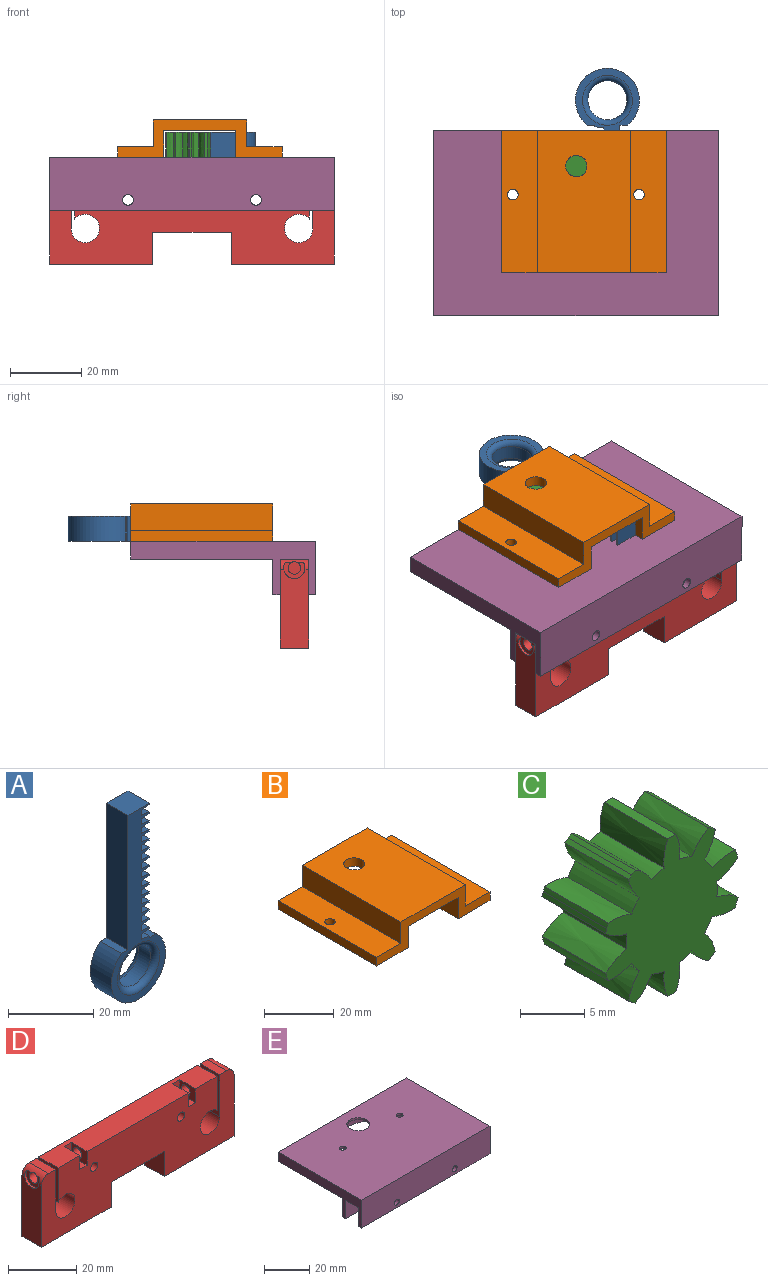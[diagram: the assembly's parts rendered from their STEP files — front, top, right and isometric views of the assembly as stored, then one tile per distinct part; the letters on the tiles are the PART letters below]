
ASSEMBLY  parts=5 mates=10
PART A: 71 faces, bbox 18x7x54.7 mm
  f0: plane 7x0.45mm, normal (1,0,0), area 3.1mm2, adj f15,f16,f60,f62
  f1: plane 7x0.45mm, normal (1,0,0), area 3.1mm2, adj f15,f16,f57,f59
  f2: plane 7x0.45mm, normal (1,0,0), area 3.2mm2, adj f15,f16,f54,f56
  f3: plane 7x0.45mm, normal (1,0,0), area 3.2mm2, adj f15,f16,f51,f53
  f4: plane 7x0.45mm, normal (1,0,0), area 3.2mm2, adj f15,f16,f48,f50
  f5: plane 7x0.45mm, normal (1,0,0), area 3.1mm2, adj f15,f16,f45,f47
  f6: plane 7x0.45mm, normal (1,0,0), area 3.1mm2, adj f15,f16,f42,f44
  f7: plane 7x0.45mm, normal (1,0,0), area 3.1mm2, adj f15,f16,f39,f41
  f8: plane 7x0.45mm, normal (1,0,0), area 3.1mm2, adj f15,f16,f36,f38
  f9: plane 7x0.45mm, normal (1,0,0), area 3.2mm2, adj f15,f16,f33,f35
  f10: plane 7x0.45mm, normal (1,0,0), area 3.1mm2, adj f15,f16,f30,f32
  f11: plane 7x0.45mm, normal (1,0,0), area 3.1mm2, adj f15,f16,f27,f29
  f12: plane 7x0.45mm, normal (1,0,0), area 3.1mm2, adj f15,f16,f24,f26
  f13: plane 7x0.45mm, normal (1,0,0), area 3.2mm2, adj f15,f16,f21,f23
  f14: plane 7x0.45mm, normal (1,0,0), area 3.1mm2, adj f15,f16,f20,f66
  f15: plane 54.7x18mm, normal (0,1,0), area 288.5mm2, adj f0,f1,f2,f3,f4,f5,f6,f7
  f16: plane 54.7x18mm, normal (0,-1,0), area 288.5mm2, adj f0,f1,f2,f3,f4,f5,f6,f7
  f17: plane 7x0.45mm, normal (1,0,0), area 3.1mm2, adj f15,f16,f19,f63
  f18: plane 38.7x7mm, normal (-1,0,0), area 270.9mm2, adj f15,f16,f19,f65
  f19: plane 7x7mm, normal (0,0,1), area 49mm2, adj f15,f16,f17,f18
  f20: plane 7x2.5mm, normal (0.12,0,0.99), area 17.6mm2, adj f14,f15,f16,f22
  f21: plane 7x2.5mm, normal (0.12,0,-0.99), area 17.6mm2, adj f13,f15,f16,f22
  f22: plane 7x1.5mm, normal (1,0,0), area 10.5mm2, adj f15,f16,f20,f21
  f23: plane 7x2.5mm, normal (0.12,0,0.99), area 17.6mm2, adj f13,f15,f16,f25
  f24: plane 7x2.5mm, normal (0.12,0,-0.99), area 17.6mm2, adj f12,f15,f16,f25
  f25: plane 7x1.5mm, normal (1,0,0), area 10.5mm2, adj f15,f16,f23,f24
  f26: plane 7x2.5mm, normal (0.12,0,0.99), area 17.6mm2, adj f12,f15,f16,f28
  f27: plane 7x2.5mm, normal (0.12,0,-0.99), area 17.6mm2, adj f11,f15,f16,f28
  f28: plane 7x1.5mm, normal (1,0,0), area 10.5mm2, adj f15,f16,f26,f27
  f29: plane 7x2.5mm, normal (0.12,0,0.99), area 17.6mm2, adj f11,f15,f16,f31
  f30: plane 7x2.5mm, normal (0.12,0,-0.99), area 17.6mm2, adj f10,f15,f16,f31
  f31: plane 7x1.5mm, normal (1,0,0), area 10.5mm2, adj f15,f16,f29,f30
  f32: plane 7x2.5mm, normal (0.12,0,0.99), area 17.6mm2, adj f10,f15,f16,f34
  f33: plane 7x2.5mm, normal (0.12,0,-0.99), area 17.6mm2, adj f9,f15,f16,f34
  f34: plane 7x1.5mm, normal (1,0,0), area 10.5mm2, adj f15,f16,f32,f33
  f35: plane 7x2.5mm, normal (0.12,0,0.99), area 17.6mm2, adj f9,f15,f16,f37
  f36: plane 7x2.5mm, normal (0.12,0,-0.99), area 17.6mm2, adj f8,f15,f16,f37
  f37: plane 7x1.5mm, normal (1,0,0), area 10.5mm2, adj f15,f16,f35,f36
  f38: plane 7x2.5mm, normal (0.12,0,0.99), area 17.6mm2, adj f8,f15,f16,f40
  f39: plane 7x2.5mm, normal (0.12,0,-0.99), area 17.6mm2, adj f7,f15,f16,f40
  f40: plane 7x1.5mm, normal (1,0,0), area 10.5mm2, adj f15,f16,f38,f39
  f41: plane 7x2.5mm, normal (0.12,0,0.99), area 17.6mm2, adj f7,f15,f16,f43
  f42: plane 7x2.5mm, normal (0.12,0,-0.99), area 17.6mm2, adj f6,f15,f16,f43
  f43: plane 7x1.5mm, normal (1,0,0), area 10.5mm2, adj f15,f16,f41,f42
  f44: plane 7x2.5mm, normal (0.12,0,0.99), area 17.6mm2, adj f6,f15,f16,f46
  f45: plane 7x2.5mm, normal (0.12,0,-0.99), area 17.6mm2, adj f5,f15,f16,f46
  f46: plane 7x1.5mm, normal (1,0,0), area 10.5mm2, adj f15,f16,f44,f45
  f47: plane 7x2.5mm, normal (0.12,0,0.99), area 17.6mm2, adj f5,f15,f16,f49
  f48: plane 7x2.5mm, normal (0.12,0,-0.99), area 17.6mm2, adj f4,f15,f16,f49
  f49: plane 7x1.5mm, normal (1,0,0), area 10.5mm2, adj f15,f16,f47,f48
  f50: plane 7x2.5mm, normal (0.12,0,0.99), area 17.6mm2, adj f4,f15,f16,f52
  f51: plane 7x2.5mm, normal (0.12,0,-0.99), area 17.6mm2, adj f3,f15,f16,f52
  f52: plane 7x1.5mm, normal (1,0,0), area 10.5mm2, adj f15,f16,f50,f51
  f53: plane 7x2.5mm, normal (0.12,0,0.99), area 17.6mm2, adj f3,f15,f16,f55
  f54: plane 7x2.5mm, normal (0.12,0,-0.99), area 17.6mm2, adj f2,f15,f16,f55
  f55: plane 7x1.5mm, normal (1,0,0), area 10.5mm2, adj f15,f16,f53,f54
  f56: plane 7x2.5mm, normal (0.12,0,0.99), area 17.6mm2, adj f2,f15,f16,f58
  f57: plane 7x2.5mm, normal (0.12,0,-0.99), area 17.6mm2, adj f1,f15,f16,f58
  f58: plane 7x1.5mm, normal (1,0,0), area 10.5mm2, adj f15,f16,f56,f57
  f59: plane 7x2.5mm, normal (0.12,0,0.99), area 17.6mm2, adj f1,f15,f16,f61
  f60: plane 7x2.5mm, normal (0.12,0,-0.99), area 17.6mm2, adj f0,f15,f16,f61
  f61: plane 7x1.5mm, normal (1,0,0), area 10.5mm2, adj f15,f16,f59,f60
  f62: plane 7x2.5mm, normal (0.12,0,0.99), area 17.6mm2, adj f0,f15,f16,f64
  f63: plane 7x2.5mm, normal (0.12,0,-0.99), area 17.6mm2, adj f15,f16,f17,f64
  f64: plane 7x1.5mm, normal (1,0,0), area 10.5mm2, adj f15,f16,f62,f63
  f65: plane 7x2.16mm, normal (0,0,1), area 15.1mm2, adj f15,f16,f18,f68
  f66: plane 7x2.16mm, normal (0,0,1), area 15.1mm2, adj f14,f15,f16,f68
  f67: cylinder r=5.5mm len=11mm, axis (0,-1,0), area 138.2mm2, adj f69,f70
  f68: cylinder r=9mm len=18mm, axis (0,-1,0), area 310.2mm2, adj f15,f16,f65,f66
  f69: torus R=7mm, axis (0,-1,0), area 89.5mm2, adj f16,f67
  f70: torus R=7mm, axis (0,-1,0), area 89.5mm2, adj f15,f67
PART B: 17 faces, bbox 46.3x40x10.5 mm
  f0: plane 40x3mm, normal (-1,0,0), area 120mm2, adj f1,f11,f12,f13
  f1: plane 40x13mm, normal (0,0,-1), area 512.9mm2, adj f0,f2,f12,f13,f15
  f2: plane 40x7.5mm, normal (1,0,0), area 300mm2, adj f1,f3,f12,f13
  f3: plane 40x20.25mm, normal (0,0,-1), area 781.7mm2, adj f2,f4,f12,f13,f14
  f4: plane 40x7.5mm, normal (-1,0,0), area 300mm2, adj f3,f5,f12,f13
  f5: plane 40x13mm, normal (0,0,-1), area 512.9mm2, adj f4,f6,f12,f13,f16
  f6: plane 40x3mm, normal (1,0,0), area 120mm2, adj f5,f7,f12,f13
  f7: plane 40x10mm, normal (0,0,1), area 392.9mm2, adj f6,f8,f12,f13,f16
  f8: plane 40x7.5mm, normal (1,0,0), area 300mm2, adj f7,f9,f12,f13
  f9: plane 40x26.25mm, normal (0,0,1), area 1021.7mm2, adj f8,f10,f12,f13,f14
  f10: plane 40x7.5mm, normal (-1,0,0), area 300mm2, adj f9,f11,f12,f13
  f11: plane 40x10mm, normal (0,0,1), area 392.9mm2, adj f0,f10,f12,f13,f15
  f12: plane 46.25x10.5mm, normal (0,-1,0), area 183.8mm2, adj f0,f1,f2,f3,f4,f5,f6,f7
  f13: plane 46.25x10.5mm, normal (0,1,0), area 183.7mm2, adj f0,f1,f2,f3,f4,f5,f6,f7
  f14: cylinder r=3mm len=6mm, axis (0,0,1), area 56.5mm2, adj f3,f9
  f15: cylinder r=1.5mm len=3mm, axis (0,0,-1), area 28.3mm2, adj f1,f11
  f16: cylinder r=1.5mm len=3mm, axis (0,0,-1), area 28.3mm2, adj f5,f7
PART C: 45 faces, bbox 14.5x7x15 mm
  f0: extruded ~7x2.3mm, area 18.3mm2, adj f1,f42,f43,f44
  f1: cylinder r=7.5mm len=7mm, axis (0,1,0), area 6.4mm2, adj f0,f2,f43,f44
  f2: extruded ~7x1.84mm, area 18.3mm2, adj f1,f3,f43,f44
  f3: cylinder r=5mm len=7mm, axis (0,1,0), area 10mm2, adj f2,f4,f43,f44
  f4: extruded ~7x2.56mm, area 18.3mm2, adj f3,f5,f43,f44
  f5: cylinder r=7.5mm len=7mm, axis (0,1,0), area 6.4mm2, adj f4,f6,f43,f44
  f6: extruded ~7x2.56mm, area 18.3mm2, adj f5,f7,f43,f44
  f7: cylinder r=5mm len=7mm, axis (0,1,0), area 10mm2, adj f6,f8,f43,f44
  f8: extruded ~7x1.84mm, area 18.3mm2, adj f7,f9,f43,f44
  f9: cylinder r=7.5mm len=7mm, axis (0,1,0), area 6.4mm2, adj f8,f10,f43,f44
  f10: extruded ~7x2.3mm, area 18.3mm2, adj f9,f11,f43,f44
  f11: cylinder r=5mm len=7mm, axis (0,1,0), area 10mm2, adj f10,f12,f43,f44
  f12: extruded ~7x2.56mm, area 18.3mm2, adj f11,f13,f43,f44
  f13: cylinder r=7.5mm len=7mm, axis (0,1,0), area 3.2mm2, adj f12,f14,f43,f44
  f14: plane 7x0.43mm, normal (0.95,0,-0.31), area 3.1mm2, adj f13,f15,f43,f44
  f15: extruded ~7x2.32mm, area 18.4mm2, adj f14,f16,f43,f44
  f16: cylinder r=5mm len=7mm, axis (0,1,0), area 10mm2, adj f15,f17,f43,f44
  f17: extruded ~7x2.31mm, area 18.3mm2, adj f16,f18,f43,f44
  f18: cylinder r=7.5mm len=7mm, axis (0,1,0), area 6.4mm2, adj f17,f19,f43,f44
  f19: extruded ~7x2.56mm, area 18.3mm2, adj f18,f20,f43,f44
  f20: cylinder r=5mm len=7mm, axis (0,1,0), area 10mm2, adj f19,f21,f43,f44
  f21: extruded ~7x2.3mm, area 18.3mm2, adj f20,f22,f43,f44
  f22: cylinder r=7.5mm len=7mm, axis (0,1,0), area 6.4mm2, adj f21,f23,f43,f44
  f23: extruded ~7x1.84mm, area 18.3mm2, adj f22,f24,f43,f44
  f24: cylinder r=5mm len=7mm, axis (0,1,0), area 10mm2, adj f23,f25,f43,f44
  f25: extruded ~7x2.57mm, area 18.4mm2, adj f24,f26,f43,f44
  f26: plane 7x0.9mm, normal (0,0,1), area 6.3mm2, adj f25,f27,f43,f44
  f27: extruded ~7x2.57mm, area 18.4mm2, adj f26,f28,f43,f44
  f28: cylinder r=5mm len=7mm, axis (0,1,0), area 10mm2, adj f27,f29,f43,f44
  f29: extruded ~7x1.84mm, area 18.3mm2, adj f28,f30,f43,f44
  f30: cylinder r=7.5mm len=7mm, axis (0,1,0), area 3.2mm2, adj f29,f31,f43,f44
  f31: plane 7x0.36mm, normal (-0.59,0,0.81), area 3.2mm2, adj f30,f32,f43,f44
  f32: extruded ~7x2.32mm, area 18.4mm2, adj f31,f33,f43,f44
  f33: cylinder r=5mm len=7mm, axis (0,1,0), area 10mm2, adj f32,f34,f43,f44
  f34: extruded ~7x2.56mm, area 18.3mm2, adj f33,f35,f43,f44
  f35: cylinder r=7.5mm len=7mm, axis (0,1,0), area 3.2mm2, adj f34,f36,f43,f44
  f36: plane 7x0.43mm, normal (-0.95,0,0.31), area 3.1mm2, adj f35,f37,f43,f44
  f37: extruded ~7x2.32mm, area 18.4mm2, adj f36,f38,f43,f44
  f38: cylinder r=5mm len=7mm, axis (0,1,0), area 10mm2, adj f37,f39,f43,f44
  f39: extruded ~7x2.31mm, area 18.3mm2, adj f38,f40,f43,f44
  f40: cylinder r=7.5mm len=7mm, axis (0,1,0), area 6.4mm2, adj f39,f41,f43,f44
  f41: extruded ~7x2.56mm, area 18.3mm2, adj f40,f42,f43,f44
  f42: cylinder r=5mm len=7mm, axis (0,1,0), area 10mm2, adj f0,f41,f43,f44
  f43: plane 15x14.54mm, normal (0,-1,0), area 117.2mm2, adj f0,f1,f2,f3,f4,f5,f6,f7
  f44: plane 15x14.54mm, normal (0,1,0), area 117.2mm2, adj f0,f1,f2,f3,f4,f5,f6,f7
PART D: 42 faces, bbox 80x8x25 mm
  f0: cylinder r=3mm len=8mm, axis (0,-1,0), area 24.4mm2, adj f2,f3,f17,f18,f36,f40,f41
  f1: plane 22x8mm, normal (-1,0,0), area 164.8mm2, adj f2,f3,f12,f33,f34
  f2: plane 80x25mm, normal (0,-1,0), area 1627.1mm2, adj f0,f1,f4,f5,f6,f7,f8,f9
  f3: plane 80x25mm, normal (0,1,0), area 1657.1mm2, adj f0,f1,f4,f5,f6,f7,f8,f9
  f4: plane 66x8mm, normal (0,0,1), area 489mm2, adj f2,f3,f7,f8,f19,f20,f22,f23
  f5: plane 15x8mm, normal (-1,0,0), area 110.4mm2, adj f2,f3,f6,f18,f36
  f6: cylinder r=4mm len=8mm, axis (0,1,0), area 177.9mm2, adj f2,f3,f5,f7
  f7: plane 12.35x8mm, normal (1,0,0), area 89.2mm2, adj f2,f3,f4,f6,f39
  f8: plane 12.35x8mm, normal (-1,0,0), area 89.2mm2, adj f2,f3,f4,f9,f31
  f9: cylinder r=4mm len=8mm, axis (0,1,0), area 177.9mm2, adj f2,f3,f8,f10
  f10: plane 15x8mm, normal (1,0,0), area 110.4mm2, adj f2,f3,f9,f11,f32
  f11: plane 8x3mm, normal (0,0,1), area 24mm2, adj f2,f3,f10,f33
  f12: plane 29x8mm, normal (0,0,-1), area 232mm2, adj f1,f2,f3,f13
  f13: plane 9x8mm, normal (1,0,0), area 72mm2, adj f2,f3,f12,f14
  f14: plane 22x8mm, normal (0,0,-1), area 176mm2, adj f2,f3,f13,f15
  f15: plane 9x8mm, normal (-1,0,0), area 72mm2, adj f2,f3,f14,f16
  f16: plane 29x8mm, normal (0,0,-1), area 232mm2, adj f2,f3,f15,f17
  f17: plane 22x8mm, normal (1,0,0), area 164.8mm2, adj f0,f2,f3,f16,f40
  f18: plane 8x3mm, normal (0,0,1), area 24mm2, adj f0,f2,f3,f5
  f19: plane 6.5x5mm, normal (-1,0,0), area 22.9mm2, adj f2,f4,f21,f22,f39
  f20: plane 6.5x5mm, normal (1,0,0), area 22.9mm2, adj f2,f4,f21,f22,f38
  f21: plane 6.5x3mm, normal (0,0,1), area 19.5mm2, adj f2,f19,f20,f22
  f22: plane 5x3mm, normal (0,-1,0), area 15mm2, adj f4,f19,f20,f21
  f23: plane 6.5x5mm, normal (1,0,0), area 22.9mm2, adj f2,f4,f24,f26,f31
  f24: plane 6.5x3mm, normal (0,0,1), area 19.5mm2, adj f2,f23,f25,f26
  f25: plane 6.5x5mm, normal (-1,0,0), area 22.9mm2, adj f2,f4,f24,f26,f30
  f26: plane 5x3mm, normal (0,-1,0), area 15mm2, adj f4,f23,f24,f25
  f27: cylinder r=1.5mm len=8mm, axis (0,-1,0), area 75.4mm2, adj f2,f3
  f28: cylinder r=1.5mm len=8mm, axis (0,-1,0), area 75.4mm2, adj f2,f3
  f29: plane 3.5x3.5mm, normal (-1,0,0), area 9.6mm2, adj f30
  f30: cylinder r=1.75mm len=6mm, axis (-1,0,0), area 66mm2, adj f25,f29
  f31: cylinder r=1.75mm len=9mm, axis (-1,0,0), area 99mm2, adj f8,f23
  f32: cylinder r=1.75mm len=5.2mm, axis (-1,0,0), area 56.9mm2, adj f10,f33,f35
  f33: cylinder r=3mm len=8mm, axis (0,1,0), area 24.4mm2, adj f1,f2,f3,f11,f32,f34,f35
  f34: cylinder r=3mm len=6mm, axis (-1,0,0), area 9mm2, adj f1,f33,f35
  f35: plane 6x4.54mm, normal (-1,0,0), area 13.6mm2, adj f32,f33,f34
  f36: cylinder r=1.75mm len=5.2mm, axis (1,0,0), area 56.9mm2, adj f0,f5,f41
  f37: plane 3.5x3.5mm, normal (1,0,0), area 9.6mm2, adj f38
  f38: cylinder r=1.75mm len=6mm, axis (1,0,0), area 66mm2, adj f20,f37
  f39: cylinder r=1.75mm len=9mm, axis (1,0,0), area 99mm2, adj f7,f19
  f40: cylinder r=3mm len=6mm, axis (1,0,0), area 9mm2, adj f0,f17,f41
  f41: plane 6x4.54mm, normal (1,0,0), area 13.6mm2, adj f0,f36,f40
PART E: 28 faces, bbox 80x52x15 mm
  f0: plane 80x10mm, normal (0,1,0), area 785.9mm2, adj f4,f7,f9,f23,f26,f27
  f1: plane 80x15mm, normal (0,-1,0), area 1185.9mm2, adj f4,f5,f9,f22,f24,f25
  f2: plane 80x10mm, normal (0,-1,0), area 785.9mm2, adj f4,f9,f21,f23,f26,f27
  f3: plane 80x10mm, normal (0,1,0), area 785.9mm2, adj f4,f9,f21,f22,f24,f25
  f4: plane 52x15mm, normal (1,0,0), area 300mm2, adj f0,f1,f2,f3,f5,f7,f10,f21
  f5: plane 80x52mm, normal (0,0,1), area 4067.3mm2, adj f1,f4,f8,f9,f10,f19,f20
  f6: plane 43x30mm, normal (0,0,-1), area 702mm2, adj f8,f11,f12,f13,f14,f15,f16,f17
  f7: plane 80x40mm, normal (0,0,-1), area 2405.3mm2, adj f0,f4,f9,f10,f11,f12,f13,f14
  f8: cylinder r=5mm len=10mm, axis (0,0,-1), area 31.4mm2, adj f5,f6
  f9: plane 52x15mm, normal (-1,0,0), area 300mm2, adj f0,f1,f2,f3,f5,f7,f10,f21
  f10: plane 80x5mm, normal (0,1,0), area 400mm2, adj f4,f5,f7,f9
  f11: plane 4x3.23mm, normal (0,1,0), area 12.9mm2, adj f6,f7,f12,f18
  f12: cylinder r=3.75mm len=7.5mm, axis (0,0,-1), area 47.1mm2, adj f6,f7,f11,f13
  f13: plane 4x3.23mm, normal (0,-1,0), area 12.9mm2, adj f6,f7,f12,f14
  f14: cylinder r=15mm len=29.05mm, axis (0,0,-1), area 158.2mm2, adj f6,f7,f13,f15
  f15: plane 4x3.23mm, normal (0,-1,0), area 12.9mm2, adj f6,f7,f14,f16
  f16: cylinder r=3.75mm len=7.5mm, axis (0,0,-1), area 47.1mm2, adj f6,f7,f15,f17
  f17: plane 4x3.23mm, normal (0,1,0), area 12.9mm2, adj f6,f7,f16,f18
  f18: cylinder r=15mm len=29.05mm, axis (0,0,-1), area 158.2mm2, adj f6,f7,f11,f17
  f19: cylinder r=1.5mm len=3mm, axis (0,0,-1), area 9.4mm2, adj f5,f6
  f20: cylinder r=1.5mm len=3mm, axis (0,0,-1), area 9.4mm2, adj f5,f6
  f21: plane 80x8mm, normal (0,0,-1), area 640mm2, adj f2,f3,f4,f9
  f22: plane 80x2mm, normal (0,0,-1), area 160mm2, adj f1,f3,f4,f9
  f23: plane 80x2mm, normal (0,0,-1), area 160mm2, adj f0,f2,f4,f9
  f24: cylinder r=1.5mm len=3mm, axis (0,-1,0), area 18.8mm2, adj f1,f3
  f25: cylinder r=1.5mm len=3mm, axis (0,-1,0), area 18.8mm2, adj f1,f3
  f26: cylinder r=1.5mm len=3mm, axis (0,-1,0), area 18.8mm2, adj f0,f2
  f27: cylinder r=1.5mm len=3mm, axis (0,-1,0), area 18.8mm2, adj f0,f2
PLACE A rot(axis=(0,-0.71,0.71),180deg) t=(21.1,57.29,32.26)mm
PLACE B t=(14.47,55.78,32.51)mm
PLACE C rot(axis=(-0.67,0.53,-0.53),112.6deg) t=(12.26,45.78,28.76)mm
PLACE D t=(12.26,13.78,11.26)mm fixed
PLACE E t=(12.26,15.78,23.76)mm
MATE planar A.f15 <-> E.f5  axis (0,0,-1) through (21.64,46.13,28.76)mm
MATE cylindrical E.f24 <-> D.f27  axis (0,-1,0) through (30.26,3.78,16.76)mm
MATE planar A.f18 <-> B.f4  axis (1,0,0) through (24.6,37.94,32.26)mm
MATE planar E.f3 <-> D.f2  axis (0,1,0) through (12.26,5.78,18.8)mm
MATE cylindrical C.f1 <-> E.f8  axis (0,0,-1) through (12.26,45.78,28.76)mm
MATE planar C.f9 <-> E.f5  axis (0,0,-1) through (12.26,45.78,28.76)mm
MATE cylindrical B.f16 <-> E.f16  axis (0,0,-1) through (30.01,37.78,30.26)mm
MATE planar E.f5 <-> B.f5  axis (0,0,1) through (12.26,29.45,28.76)mm
MATE cylindrical E.f12 <-> B.f15  axis (0,0,-1) through (-5.49,37.78,28.26)mm
MATE cylindrical E.f25 <-> D.f28  axis (0,-1,0) through (-5.74,3.78,16.76)mm
